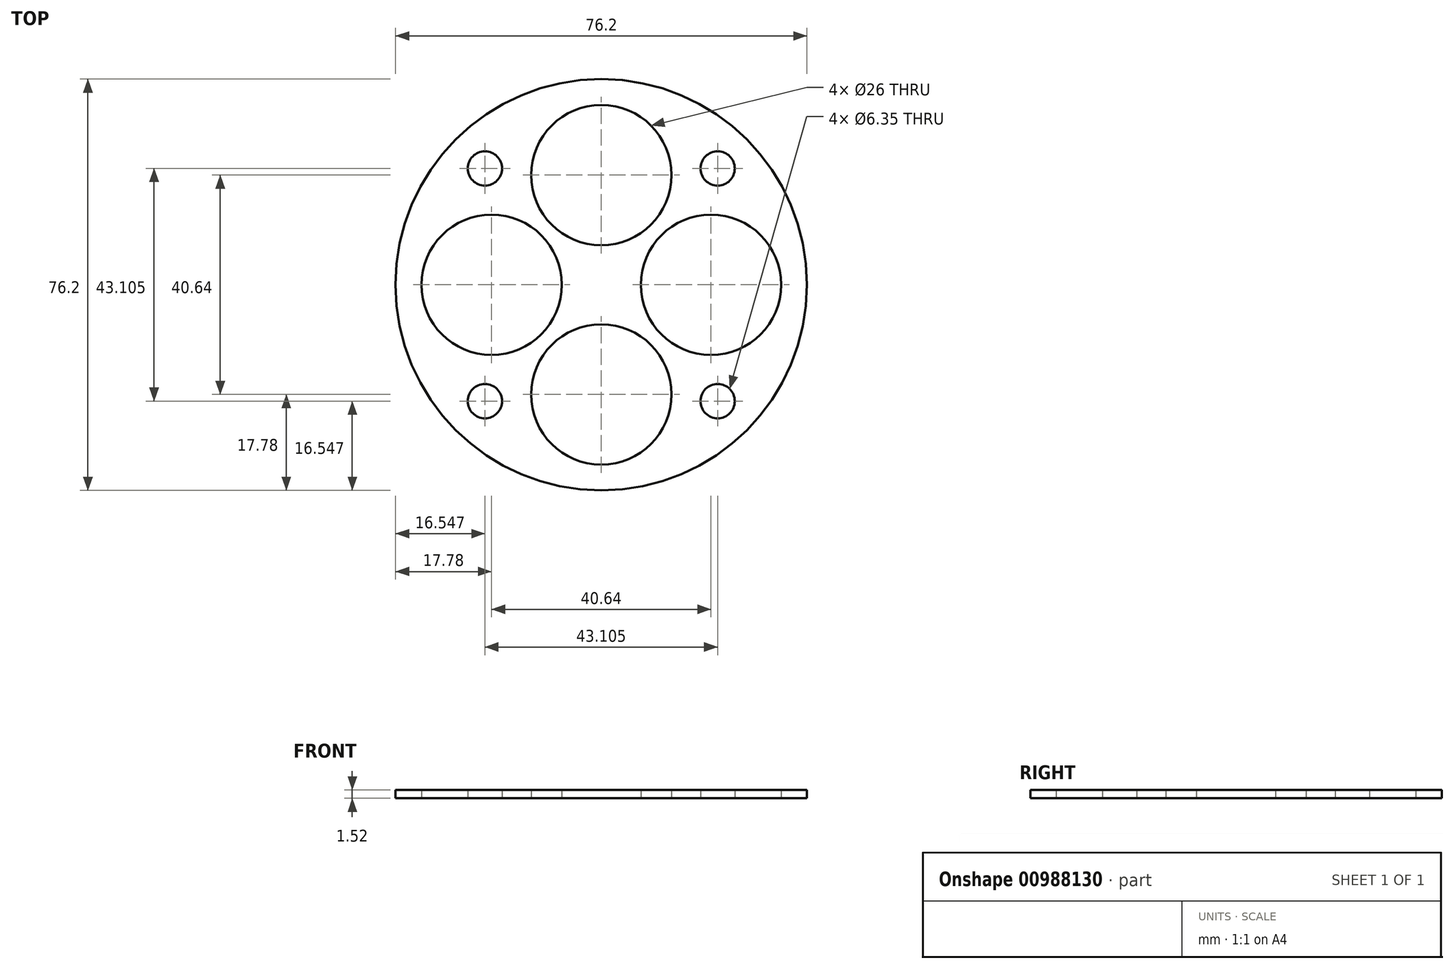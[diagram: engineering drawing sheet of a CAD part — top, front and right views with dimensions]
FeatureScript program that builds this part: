
annotation { "Feature Type Name" : "Feature", "Feature Type Description" : "" }
export const myFeature = defineFeature(function(context is Context, id is Id, definition is map)
    precondition{}
    {
        {
            var Q0;
            Q0=qCreatedBy(makeId("Top.planeOp"),FACE);
            var sketch = newSketch(context, id + "F0", { "sketchPlane" : qUnion([Q0])});
            skCircle(sketch, "E0", {"center": v(0, 0) * mm, "radius": 38.1 * mm});
            skCircle(sketch, "E1", {"center": v(0, 20.32) * mm, "radius": 13 * mm});
            skLineSegment(sketch, "E2", {"start": v(0, 20.32) * mm, "end": v(0, 0) * mm, "construction": true});
            skCircle(sketch, "E3", {"center": v(21.55, 21.55) * mm, "radius": 3.18 * mm});
            skLineSegment(sketch, "E4", {"start": v(0, 0) * mm, "end": v(21.55, 21.55) * mm, "construction": true});
            skCircle(sketch, "E5", {"center": v(21.55, 21.55) * mm, "radius": 5.55 * mm, "construction": true});
            skCircle(sketch, "E6.1.0", {"center": v(-20.32, 0) * mm, "radius": 13 * mm});
            skCircle(sketch, "E6.1.1", {"center": v(-21.55, 21.55) * mm, "radius": 3.18 * mm});
            skCircle(sketch, "E6.2.0", {"center": v(0, -20.32) * mm, "radius": 13 * mm});
            skCircle(sketch, "E6.2.1", {"center": v(-21.55, -21.55) * mm, "radius": 3.18 * mm});
            skCircle(sketch, "E6.3.0", {"center": v(20.32, 0) * mm, "radius": 13 * mm});
            skCircle(sketch, "E6.3.1", {"center": v(21.55, -21.55) * mm, "radius": 3.18 * mm});
            skSolve(sketch);
        }
        {
            var Q0;
            Q0=makeQuery(id+"F0.imprint","IMPRINT",FACE,{"disambiguationData":[TD([[makeQuery(id+"F0.imprint","IMPRINT",EDGE,{"derivedFrom":sQuery(id+"F0.wireOp",EDGE,"E0")}),1.0]])]});
            extrude(context, id + "F1", {"entities" : qUnion([Q0]), "depth" : 1.52 * mm, "offsetDistance" : 25.4 * mm});
        }
    });
